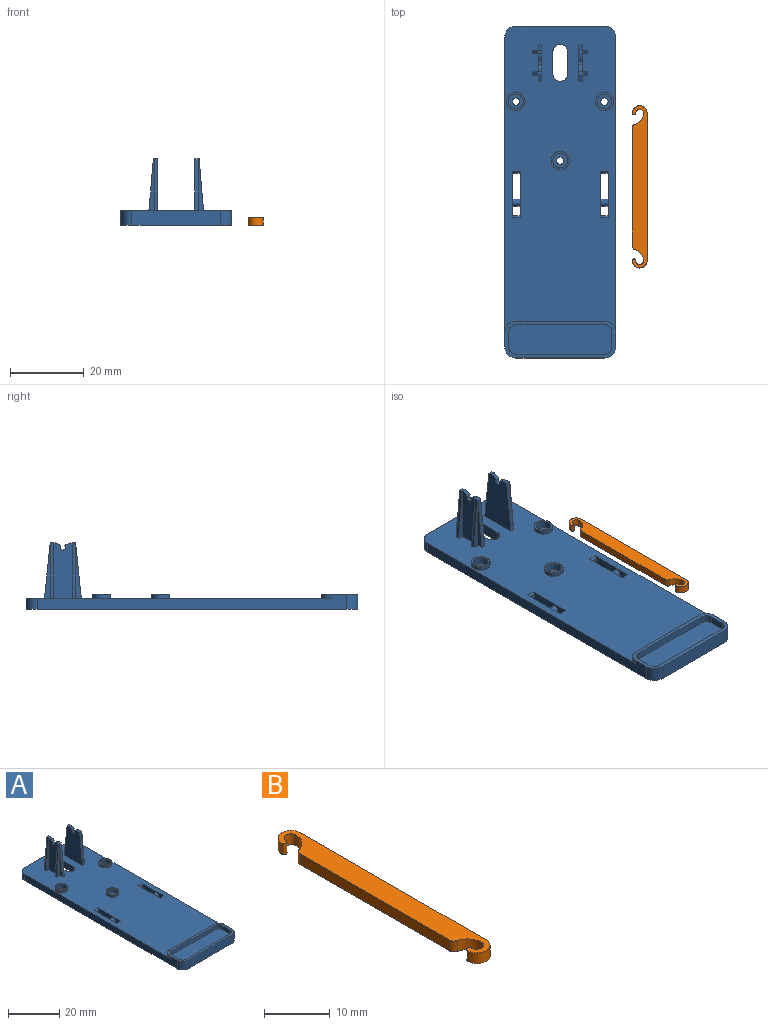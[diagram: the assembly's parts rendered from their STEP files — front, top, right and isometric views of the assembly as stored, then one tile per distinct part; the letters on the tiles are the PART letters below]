
ASSEMBLY  parts=2 mates=1
PART A: 94 faces, bbox 30x90x18 mm
  f0: plane 83x30mm, normal (0,0,1), area 2225.1mm2, adj f2,f3,f4,f5,f8,f10,f11,f14
  f1: plane 90x30mm, normal (0,0,-1), area 2592.5mm2, adj f8,f9,f10,f11,f12,f13,f14,f15
  f2: plane 15x4.95mm, normal (-1,0,0), area 70.9mm2, adj f0,f40,f43,f44,f51,f56
  f3: plane 15x1.58mm, normal (-1,0,0), area 11.8mm2, adj f0,f29,f52
  f4: plane 15x1.58mm, normal (1,0,0), area 11.8mm2, adj f0,f36,f50
  f5: plane 15x4.95mm, normal (1,0,0), area 70.9mm2, adj f0,f39,f41,f42,f47,f48
  f6: plane 1.19x0.95mm, normal (0,0,1), area 1.1mm2, adj f30,f31,f43,f54,f55,f56
  f7: plane 1.19x0.95mm, normal (0,0,1), area 1.1mm2, adj f34,f35,f42,f45,f46,f47
  f8: plane 84x4mm, normal (-1,0,0), area 256mm2, adj f0,f1,f12,f15,f18,f27
  f9: plane 24x4mm, normal (0,-1,0), area 96mm2, adj f1,f12,f13,f27
  f10: plane 84x4mm, normal (1,0,0), area 256mm2, adj f0,f1,f13,f14,f16,f27
  f11: plane 24x3mm, normal (0,1,0), area 72mm2, adj f0,f1,f14,f15
  f12: cylinder r=3mm len=4mm, axis (0,0,-1), area 18.8mm2, adj f1,f8,f9,f27
  f13: cylinder r=3mm len=4mm, axis (0,0,1), area 18.8mm2, adj f1,f9,f10,f27
  f14: cylinder r=3mm len=3mm, axis (0,0,-1), area 14.1mm2, adj f0,f1,f10,f11
  f15: cylinder r=3mm len=3mm, axis (0,0,1), area 14.1mm2, adj f0,f1,f8,f11
  f16: cylinder r=3mm len=3mm, axis (0,0,-1), area 4.7mm2, adj f0,f10,f17,f27
  f17: plane 24x1mm, normal (0,1,0), area 24mm2, adj f0,f16,f18,f27
  f18: cylinder r=3mm len=3mm, axis (0,0,-1), area 4.7mm2, adj f0,f8,f17,f27
  f19: plane 4x2mm, normal (-1,0,0), area 8mm2, adj f20,f26,f27,f28
  f20: cylinder r=2mm len=2mm, axis (0,0,-1), area 6.3mm2, adj f19,f21,f27,f28
  f21: plane 24x2mm, normal (0,1,0), area 48mm2, adj f20,f22,f27,f28
  f22: cylinder r=2mm len=2mm, axis (0,0,-1), area 6.3mm2, adj f21,f23,f27,f28
  f23: plane 4x2mm, normal (1,0,0), area 8mm2, adj f22,f24,f27,f28
  f24: cylinder r=2mm len=2mm, axis (0,0,-1), area 6.3mm2, adj f23,f25,f27,f28
  f25: plane 24x2mm, normal (0,-1,0), area 48mm2, adj f24,f26,f27,f28
  f26: cylinder r=2mm len=2mm, axis (0,0,-1), area 6.3mm2, adj f19,f25,f27,f28
  f27: plane 30x10mm, normal (0,0,1), area 71.7mm2, adj f8,f9,f10,f12,f13,f16,f17,f18
  f28: plane 28x8mm, normal (0,0,1), area 220.6mm2, adj f19,f20,f21,f22,f23,f24,f25,f26
  f29: plane 15x1.58mm, normal (0,-0.99,0.1), area 15.1mm2, adj f0,f3,f30,f33
  f30: plane 15x10mm, normal (1,0,0), area 123.1mm2, adj f0,f6,f29,f31,f33,f40,f43,f44
  f31: plane 15x1.58mm, normal (0,0.99,0.1), area 15.1mm2, adj f0,f6,f30,f32
  f32: plane 15x1.58mm, normal (-1,0,0), area 11.8mm2, adj f0,f31,f55
  f33: plane 1.19x0.95mm, normal (0,0,1), area 1.1mm2, adj f29,f30,f44,f51,f52,f53
  f34: plane 15x1.58mm, normal (0,0.99,0.1), area 15.1mm2, adj f0,f7,f35,f37
  f35: plane 15x10mm, normal (-1,0,0), area 123.1mm2, adj f0,f7,f34,f36,f38,f39,f41,f42
  f36: plane 15x1.58mm, normal (0,-0.99,0.1), area 15.1mm2, adj f0,f4,f35,f38
  f37: plane 15x1.58mm, normal (1,0,0), area 11.8mm2, adj f0,f34,f45
  f38: plane 1.19x0.95mm, normal (0,0,1), area 1.1mm2, adj f35,f36,f41,f48,f49,f50
  f39: cylinder r=0.75mm len=1.5mm, axis (1,0,0), area 3.5mm2, adj f5,f35,f41,f42
  f40: cylinder r=0.75mm len=1.5mm, axis (1,0,0), area 3.5mm2, adj f2,f30,f43,f44
  f41: cylinder r=3mm len=1.95mm, axis (1,0,0), area 2.1mm2, adj f5,f35,f38,f39
  f42: cylinder r=3mm len=1.95mm, axis (1,0,0), area 2.1mm2, adj f5,f7,f35,f39
  f43: cylinder r=3mm len=1.95mm, axis (1,0,0), area 2.1mm2, adj f2,f6,f30,f40
  f44: cylinder r=3mm len=1.95mm, axis (1,0,0), area 2.1mm2, adj f2,f30,f33,f40
  f45: plane 15x1.5mm, normal (0,1,0), area 12.7mm2, adj f0,f7,f37,f46
  f46: plane 15x1.31mm, normal (1,0,0.09), area 14.3mm2, adj f0,f7,f45,f47
  f47: plane 15x1.5mm, normal (0,-1,0), area 12.7mm2, adj f0,f5,f7,f46
  f48: plane 15x1.5mm, normal (0,1,0), area 12.7mm2, adj f0,f5,f38,f49
  f49: plane 15x1.31mm, normal (1,0,0.09), area 14.3mm2, adj f0,f38,f48,f50
  f50: plane 15x1.5mm, normal (0,-1,0), area 12.7mm2, adj f0,f4,f38,f49
  f51: plane 15x1.5mm, normal (0,1,0), area 12.7mm2, adj f0,f2,f33,f53
  f52: plane 15x1.5mm, normal (0,-1,0), area 12.7mm2, adj f0,f3,f33,f53
  f53: plane 15x1.31mm, normal (-1,0,0.09), area 14.3mm2, adj f0,f33,f51,f52
  f54: plane 15x1.31mm, normal (-1,0,0.09), area 14.3mm2, adj f0,f6,f55,f56
  f55: plane 15x1.5mm, normal (0,1,0), area 12.7mm2, adj f0,f6,f32,f54
  f56: plane 15x1.5mm, normal (0,-1,0), area 12.7mm2, adj f0,f2,f6,f54
  f57: plane 2.15x2mm, normal (0,-1,0), area 4.3mm2, adj f63,f64,f71,f74
  f58: plane 2.15x2mm, normal (0,1,0), area 4.3mm2, adj f59,f61,f68,f70
  f59: plane 12.5x3mm, normal (-1,0,0), area 31.9mm2, adj f0,f1,f58,f60,f66,f68,f70,f72
  f60: plane 2.15x2mm, normal (0,-1,0), area 4.3mm2, adj f59,f61,f72,f73
  f61: plane 12.5x3mm, normal (1,0,0), area 31.9mm2, adj f0,f1,f58,f60,f66,f68,f70,f72
  f62: plane 2.15x2mm, normal (0,1,0), area 4.3mm2, adj f63,f64,f67,f69
  f63: plane 12.5x3mm, normal (-1,0,0), area 31.9mm2, adj f0,f1,f57,f62,f65,f67,f69,f71
  f64: plane 12.5x3mm, normal (1,0,0), area 31.9mm2, adj f0,f1,f57,f62,f65,f67,f69,f71
  f65: cylinder r=1mm len=2.15mm, axis (1,0,0), area 13.5mm2, adj f63,f64
  f66: cylinder r=1mm len=2.15mm, axis (1,0,0), area 13.5mm2, adj f59,f61
  f67: plane 2.15x0.5mm, normal (0,0.71,-0.71), area 1.5mm2, adj f1,f62,f63,f64
  f68: plane 2.15x0.5mm, normal (0,0.71,-0.71), area 1.5mm2, adj f1,f58,f59,f61
  f69: plane 2.15x0.5mm, normal (0,0.71,0.71), area 1.5mm2, adj f0,f62,f63,f64
  f70: plane 2.15x0.5mm, normal (0,0.71,0.71), area 1.5mm2, adj f0,f58,f59,f61
  f71: plane 2.15x0.5mm, normal (0,-0.71,-0.71), area 1.5mm2, adj f1,f57,f63,f64
  f72: plane 2.15x0.5mm, normal (0,-0.71,-0.71), area 1.5mm2, adj f1,f59,f60,f61
  f73: plane 2.15x0.5mm, normal (0,-0.71,0.71), area 1.5mm2, adj f0,f59,f60,f61
  f74: plane 2.15x0.5mm, normal (0,-0.71,0.71), area 1.5mm2, adj f0,f57,f63,f64
  f75: cylinder r=2mm len=4mm, axis (0,0,1), area 18.8mm2, adj f0,f1,f76,f78
  f76: plane 6x3mm, normal (-1,0,0), area 18mm2, adj f0,f1,f75,f77
  f77: cylinder r=2mm len=4mm, axis (0,0,1), area 18.8mm2, adj f0,f1,f76,f78
  f78: plane 6x3mm, normal (1,0,0), area 18mm2, adj f0,f1,f75,f77
  f79: cylinder r=1mm len=2mm, axis (0,0,1), area 12.6mm2, adj f1,f87
  f80: cylinder r=1mm len=2mm, axis (0,0,1), area 12.6mm2, adj f1,f85
  f81: cylinder r=1mm len=2mm, axis (0,0,1), area 12.6mm2, adj f1,f83
  f82: cylinder r=2mm len=4mm, axis (0,0,1), area 25.1mm2, adj f83,f91
  f83: plane 4x4mm, normal (0,0,1), area 9.4mm2, adj f81,f82
  f84: cylinder r=2mm len=4mm, axis (0,0,1), area 25.1mm2, adj f85,f89
  f85: plane 4x4mm, normal (0,0,1), area 9.4mm2, adj f80,f84
  f86: cylinder r=2mm len=4mm, axis (0,0,1), area 25.1mm2, adj f87,f93
  f87: plane 4x4mm, normal (0,0,1), area 9.4mm2, adj f79,f86
  f88: cylinder r=2.5mm len=5mm, axis (0,0,-1), area 15.7mm2, adj f0,f89
  f89: plane 5x5mm, normal (0,0,1), area 7.1mm2, adj f84,f88
  f90: cylinder r=2.5mm len=5mm, axis (0,0,-1), area 15.7mm2, adj f0,f91
  f91: plane 5x5mm, normal (0,0,1), area 7.1mm2, adj f82,f90
  f92: cylinder r=2.5mm len=5mm, axis (0,0,-1), area 15.7mm2, adj f0,f93
  f93: plane 5x5mm, normal (0,0,1), area 7.1mm2, adj f86,f92
PART B: 14 faces, bbox 4x44x2 mm
  f0: cylinder r=1.07mm len=2.15mm, axis (0,0,-1), area 6.8mm2, adj f1,f9,f10,f11
  f1: cylinder r=3.08mm len=2.98mm, axis (0,0,-1), area 8.1mm2, adj f0,f10,f11,f12
  f2: plane 32.1x2mm, normal (-1,0,0), area 64.2mm2, adj f10,f11,f12,f13
  f3: cylinder r=3.08mm len=2.98mm, axis (0,0,-1), area 8.1mm2, adj f4,f10,f11,f13
  f4: cylinder r=1.07mm len=2.15mm, axis (0,0,-1), area 6.8mm2, adj f3,f5,f10,f11
  f5: cylinder r=0.46mm len=2mm, axis (0,0,-1), area 2.9mm2, adj f4,f6,f10,f11
  f6: cylinder r=2mm len=4mm, axis (0,0,-1), area 12.6mm2, adj f5,f7,f10,f11
  f7: plane 40x2mm, normal (1,0,0), area 80mm2, adj f6,f8,f10,f11
  f8: cylinder r=2mm len=4mm, axis (0,0,-1), area 12.6mm2, adj f7,f9,f10,f11
  f9: cylinder r=0.46mm len=2mm, axis (0,0,-1), area 2.9mm2, adj f0,f8,f10,f11
  f10: plane 44x4mm, normal (0,0,1), area 154.5mm2, adj f0,f1,f2,f3,f4,f5,f6,f7
  f11: plane 44x4mm, normal (0,0,-1), area 154.5mm2, adj f0,f1,f2,f3,f4,f5,f6,f7
  f12: cylinder r=1mm len=2mm, axis (0,0,-1), area 2.6mm2, adj f1,f2,f10,f11
  f13: cylinder r=1mm len=2mm, axis (0,0,-1), area 2.6mm2, adj f2,f3,f10,f11
PLACE A t=(-71.59,24.75,-6.32)mm
PLACE B t=(21.62,1.87,-6.32)mm
MATE planar A.f1 <-> B.f11  axis (0,0,-1) through (-34.44,28.68,-6.32)mm
